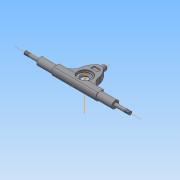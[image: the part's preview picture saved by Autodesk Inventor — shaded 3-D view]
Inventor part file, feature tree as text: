
AUTODESK INVENTOR PART (.ipt)
format: ipt  version: 2015 (Build 190159000, 159)  size: 380,928 bytes
history: native  units: in
note: dims shown in document units (in); Inventor stores cm internally (conversion verified against a paired STEP export)
features: extrude x11, sketch x8, fillet x5, other x4, plane x2, mirror x2, thread x2, projected_geometry x2, chamfer x1
ambient origin geometry x8: Origin, YZ Plane, XZ Plane, XY Plane, X Axis, Y Axis, Z Axis, Center Point
bodies: Solid1 (feature_tree)
feature tree (37):
  sketch  "Sketch1"  dims[d0=0.71in d1=0.74in]
  extrude  "Extrusion1"  Depth=0.74in
  extrude  "Extrusion2"  Depth=7.0866in TaperAngle=0.0deg
  extrude  "Extrusion3"  Depth=0.3435in
  extrude  "Extrusion4"  Depth=2.7in
  fillet  "Fillet1"  Radius=2.7in
  fillet  "Fillet2"  Radius=1.85in
  extrude  "Extrusion5"  Depth=0.06in
  fillet  "Fillet3"  Radius=0.5in
  fillet  "Fillet4"  Radius=0.5in
  sketch  "Sketch5"  dims[d15=0.06in d17=0.06in d18=0.5in d19=0.5in d20=0.0in]
  plane  "Work Plane1"
  extrude  "Extrusion6"  Depth=0.9055in
  extrude  "Extrusion7"  Depth=1.9685in
  extrude  "Extrusion8"  Depth=0.02in
  mirror  "Mirror1"
  extrude  "Extrusion9"  Depth=0.02in
  extrude  "Extrusion10"  Depth=0.02in
  thread  "Thread1"  [1 undecoded]
  thread  "Thread2"  [1 undecoded]
  fillet  "Fillet5"  Radius=0.17in
  other  "Work Axis1"
  other  "Work Axis2"
  other  "Work Point1"
  chamfer  "Chamfer1"  Distance=1.2in
  extrude  "Extrusion11"  Depth=0.02in
  plane  "Work Plane3"
  mirror  "Mirror2"
  sketch  "Sketch2"  dims[d2=0.535in d3=7.0866in d4=0.0in]
  sketch  "Sketch3"  dims[d5=0.3125in d6=0.3435in]
  projected_geometry  "Projected Loop1"
  sketch  "Sketch4"  dims[d7=3.543in d8=0.0in d9=9.9213in d10=0.0in d11=2.7in d12=2.7in d13=1.85in d14=0.0in]
  projected_geometry  "Projected Loop2"
  sketch  "Sketch6"  dims[d21=0.25in d22=0.9055in]
  sketch  "Sketch7"  dims[d23=0.0in d24=0.0in d25=1.9685in]
  other  "Work Axis3"
  sketch  "Sketch8"  dims[d26=0.7874in d27=0.635in d28=0.3175in d30=0.33in d31=0.0in d32=0.0in d33=0.225in d34=0.0in d35=0.17in d36=0.0in d37=1.2in d38=0.655in d39=0.345in d40=0.32in d41=0.05in d42=0.1in d43=0.0in d44=0.622in d45=0.58in d46=0.481in d47=0.35in d48=0.3in d49=0.025in d50=0.0in d51=0.45in d52=0.0in d53=0.45in d54=0.0in d55=0.02in d56=0.1in d57=0.125in d58=45.0deg d59=0.7087in d60=1.45in d61=0.0in]
note: 2 required parameter values undecoded (feature->parameter linkage not recoverable at this tier; creation-order binding heuristic only, values carry confidence <= 0.55)
